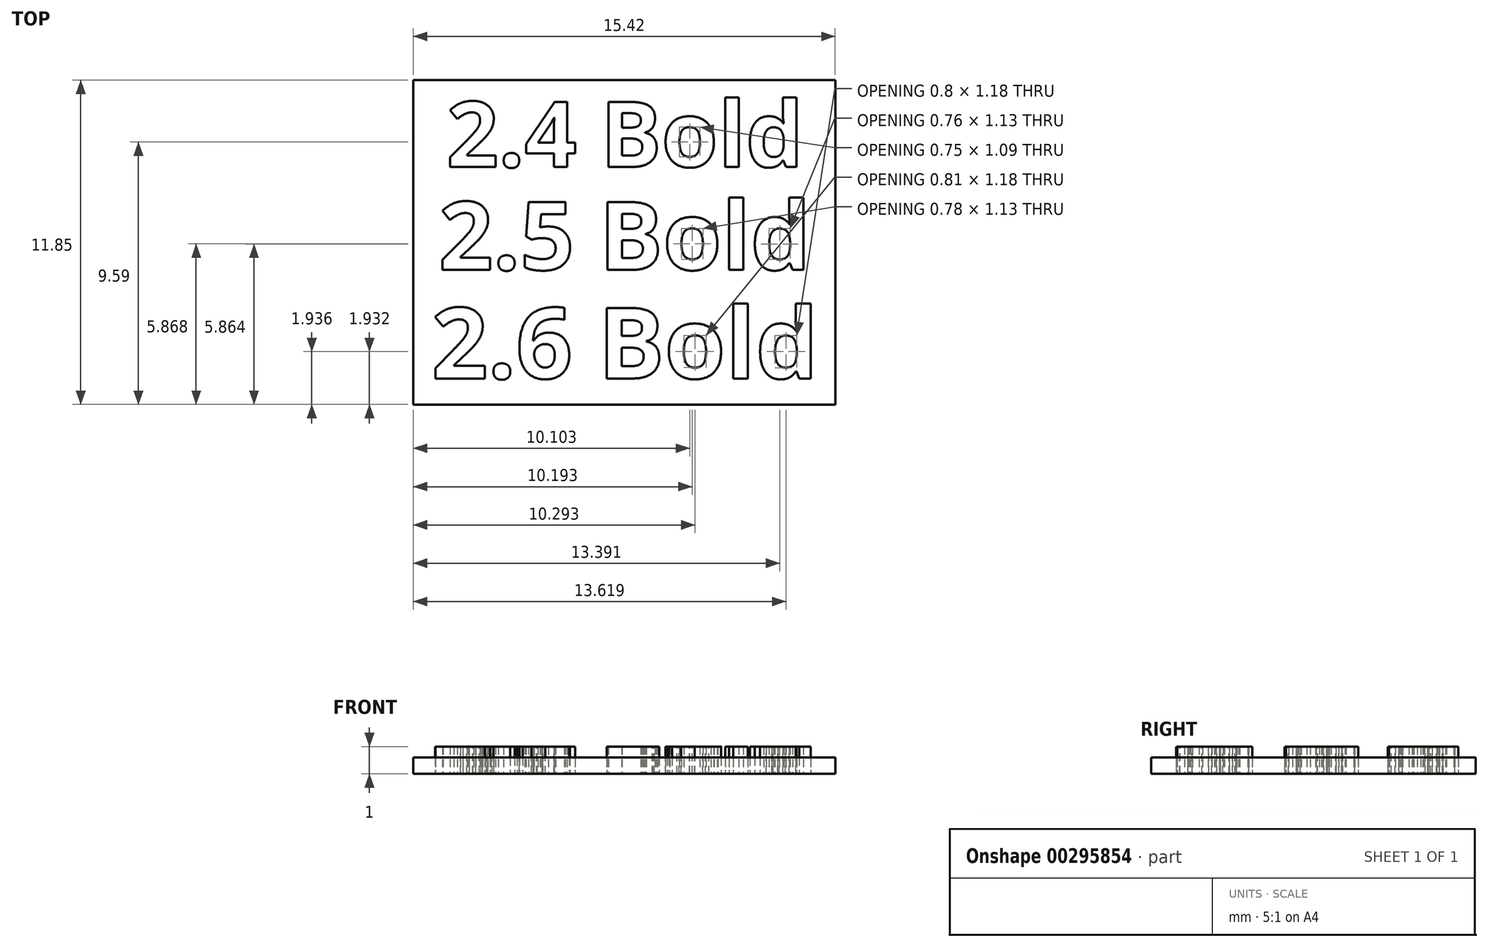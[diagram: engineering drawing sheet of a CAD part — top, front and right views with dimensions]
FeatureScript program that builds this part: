
annotation { "Feature Type Name" : "Feature", "Feature Type Description" : "" }
export const myFeature = defineFeature(function(context is Context, id is Id, definition is map)
    precondition{}
    {
        {
            var Q0;
            Q0=qCreatedBy(makeId("Top.planeOp"),FACE);
            var sketch = newSketch(context, id + "F0", { "sketchPlane" : qUnion([Q0])});
            skText(sketch, "E0", { "text": "2.4 Bold", "fontName": "OpenSans-Bold.ttf"});
            skText(sketch, "E1", { "text": "2.5 Bold", "fontName": "OpenSans-Bold.ttf"});
            skText(sketch, "E2", { "text": "2.6 Bold", "fontName": "OpenSans-Bold.ttf"});
            const initialGuessF0  = {"E0": [-0.02334, 0.0166, 1, 0, 0.0024], "E1": [-0.02362, 0.01284, 1, 0, 0.0025], "E2": [-0.02389, 0.00887, 1, 0, 0.0026]};
            skSetInitialGuess(sketch, initialGuessF0);
            skSolve(sketch);
        }
        {
            var Q0;
            Q0=qCreatedBy(makeId("Top.planeOp"),FACE);
            var sketch = newSketch(context, id + "F1", { "sketchPlane" : qUnion([Q0])});
            skLineSegment(sketch, "E3.bottom", {"start": v(-24.55, 7.92) * mm, "end": v(-9.13, 7.92) * mm});
            skLineSegment(sketch, "E3.top", {"start": v(-24.55, 19.77) * mm, "end": v(-9.13, 19.77) * mm});
            skLineSegment(sketch, "E3.left", {"start": v(-24.55, 7.92) * mm, "end": v(-24.55, 19.77) * mm});
            skLineSegment(sketch, "E3.right", {"start": v(-9.13, 7.92) * mm, "end": v(-9.13, 19.77) * mm});
            skPoint(sketch, "E4", {"position": v(-16.84, 19.77) * mm});
            skSolve(sketch);
        }
        {
            var Q0;
            Q0 = qSketchRegion(id + "F0", true);
            extrude(context, id + "F2", {"entities" : qUnion([Q0]), "depth" : 1 * mm});
        }
        {
            var Q0;
            Q0 = qSketchRegion(id + "F1", true);
            extrude(context, id + "F3", {"entities" : qUnion([Q0]), "depth" : .6 * mm});
        }
    });
